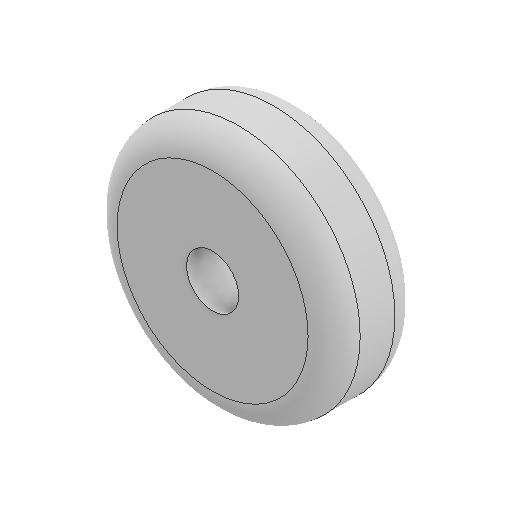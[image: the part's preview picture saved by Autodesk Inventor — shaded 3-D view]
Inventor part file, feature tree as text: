
AUTODESK INVENTOR PART (.ipt)
format: ipt  version: 2022 (Build 260153000, 153)  size: 142,848 bytes
history: native  units: mm
features: sketch x3, extrude x1, fillet x1
ambient origin geometry x8: Origin, YZ Plane, XZ Plane, XY Plane, X Axis, Y Axis, Z Axis, Center Point
bodies: Solid1 (feature_tree)
feature tree (5):
  sketch  "Sketch1"  dims[d0=112.0mm d1=24.0mm d2=40.0mm d3=0.0mm]
  extrude  "Extrusion1"  Depth=40.0mm
  fillet  "Fillet1"  Radius=40.0mm
  sketch  "Sketch3"
  sketch  "Sketch2"  dims[d4=12.0mm]
